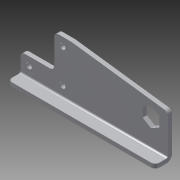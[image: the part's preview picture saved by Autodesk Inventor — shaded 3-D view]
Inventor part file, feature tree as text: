
AUTODESK INVENTOR PART (.ipt)
format: ipt  version: 2014 (Build 180170000, 170)  size: 139,776 bytes
history: native  units: in
note: dims shown in document units (in); Inventor stores cm internally (conversion verified against a paired STEP export)
features: sheet_metal_op x4, sketch x2, other x2, fillet x1
ambient origin geometry x8: Origin, YZ Plane, XZ Plane, XY Plane, X Axis, Y Axis, Z Axis, Center Point
bodies: Solid1 (feature_tree)
feature tree (9):
  sheet_metal_op  "Face1"
  sheet_metal_op  "Flange1"
  fillet  "Fillet2"  Radius=0.5in
  sketch  "Sketch1"  dims[d1=1.0in]
  other  "Plate1"
  sketch  "Sketch2"  dims[d2=1.0in d3=0.5in d4=4.375in d5=0.5in d6=0.75in d7=0.5in d8=90.0deg d9=1.125in d10=0.163in d11=0.25in d12=0.25in d13=0.7874in d15=1.0in d16=0.3937in d18=1.0in d20=0.7874in d22=1.0in d23=0.3937in d25=1.0in d27=0.125in d29=0.125in d30=0.0625in d31=0.25in d32=0.125in d33=0.5in d34=90.0deg d35=0.05in d36=0.5in d37=0.125in d38=0.125in d39=0.125in]
  other  "Plate2"
  sheet_metal_op  "Bend1"
  sheet_metal_op  "Corner1"
